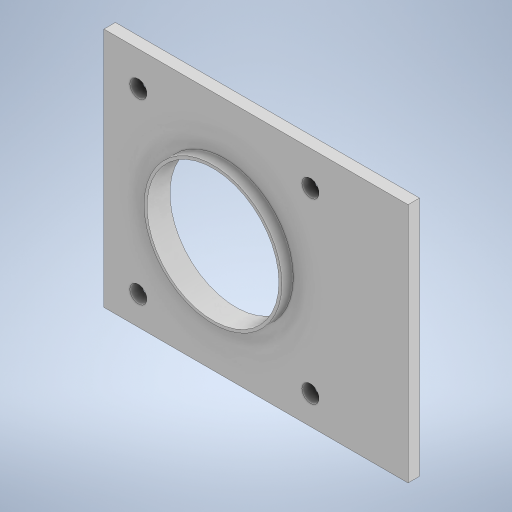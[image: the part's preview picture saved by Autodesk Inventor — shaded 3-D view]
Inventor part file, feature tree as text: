
AUTODESK INVENTOR PART (.ipt)
format: ipt  version: 2024 (Build 280153000, 153)  size: 265,728 bytes
history: native  units: mm
features: extrude x2, sketch x2, projected_geometry x1
ambient origin geometry x8: Origin, YZ Plane, XZ Plane, XY Plane, X Axis, Y Axis, Z Axis, Center Point
bodies: Solid1 (feature_tree)
feature tree (5):
  extrude  "Extrusion1"  Depth=32.0mm
  extrude  "Extrusion2"  Depth=42.0mm
  sketch  "Sketch1"  dims[d0=32.0mm d1=24.0mm]
  sketch  "Sketch2"  dims[d2=42.0mm d3=42.0mm d4=3.0mm d5=3.0mm d6=31.0mm d7=15.0mm d8=15.0mm d9=2.0mm d10=0.0mm d11=23.0mm d12=4.0mm d13=0.0mm d14=11.0mm]
  projected_geometry  "Projected Loop1"
